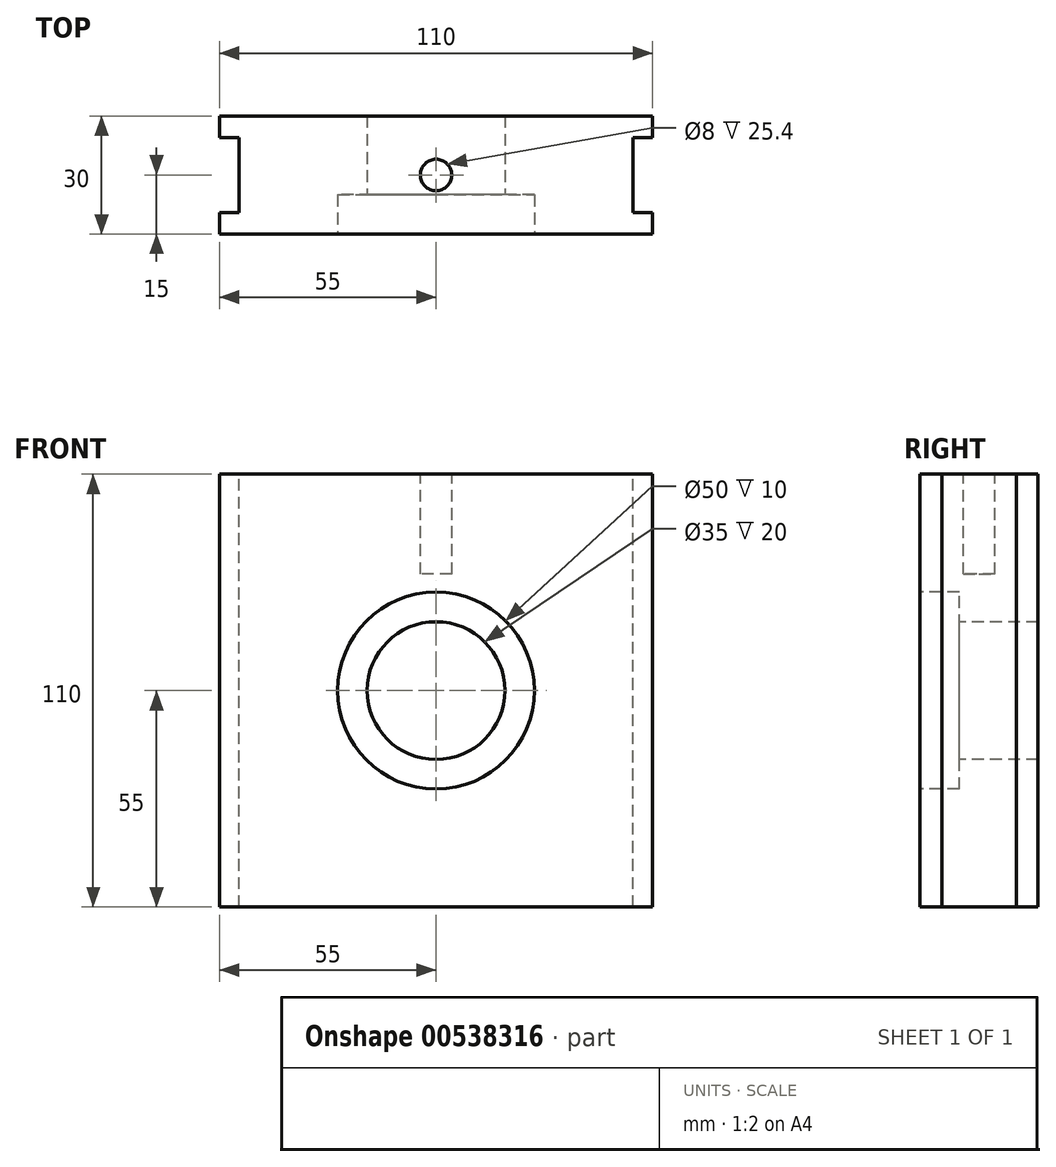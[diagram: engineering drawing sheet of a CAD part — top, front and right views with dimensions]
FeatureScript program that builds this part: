
annotation { "Feature Type Name" : "Feature", "Feature Type Description" : "" }
export const myFeature = defineFeature(function(context is Context, id is Id, definition is map)
    precondition{}
    {
        {
            var Q0;
            Q0=qCreatedBy(makeId("Front.planeOp"),FACE);
            var sketch = newSketch(context, id + "F0", { "sketchPlane" : qUnion([Q0])});
            skLineSegment(sketch, "E0.bottom", {"start": v(55, -55) * mm, "end": v(-55, -55) * mm});
            skLineSegment(sketch, "E0.top", {"start": v(55, 55) * mm, "end": v(-55, 55) * mm});
            skLineSegment(sketch, "E0.left", {"start": v(55, -55) * mm, "end": v(55, 55) * mm});
            skLineSegment(sketch, "E0.right", {"start": v(-55, -55) * mm, "end": v(-55, 55) * mm});
            skPoint(sketch, "E0.middle", {"position": v(0, 0) * mm});
            skSolve(sketch);
        }
        {
            var Q0;
            Q0 = qSketchRegion(id + "F0", true);
            extrude(context, id + "F1", {"entities" : qUnion([Q0]), "depth" : 30 * mm, "offsetDistance" : 25.4 * mm});
        }
        {
            var Q0;
            Q0=makeQuery(id+"F1.opExtrude","CAP_FACE",FACE,{"disambiguationData":[OSD([sQuery(id+"F0.wireOp",EDGE,"E0.bottom"),sQuery(id+"F0.wireOp",EDGE,"E0.top"),sQuery(id+"F0.wireOp",EDGE,"E0.left"),sQuery(id+"F0.wireOp",EDGE,"E0.right")])],"isStart":false});
            var sketch = newSketch(context, id + "F2", { "sketchPlane" : qUnion([Q0])});
            skCircle(sketch, "E1", {"center": v(0, 0) * mm, "radius": 25 * mm});
            skCircle(sketch, "E2", {"center": v(0, 0) * mm, "radius": 17.5 * mm});
            skSolve(sketch);
        }
        {
            var Q0;
            Q0 = qSketchRegion(id + "F2", true);
            var Q1;
            Q1=makeQuery(id+"F2.imprint","IMPRINT",FACE,{"disambiguationData":[TD([[makeQuery(id+"F2.imprint","IMPRINT",EDGE,{"derivedFrom":sQuery(id+"F2.wireOp",EDGE,"E1")}),1.0]])]});
            extrude(context, id + "F3", {"entities" : qUnion([Q0, Q1]), "operationType" : NewBodyOperationType.REMOVE, "oppositeDirection" : true, "depth" : 10 * mm, "offsetDistance" : 25.4 * mm});
        }
        {
            var Q0;
            Q0=makeQuery(id+"F3.boolean.opBoolean","SPLIT",FACE,{"disambiguationData":[TD([makeQuery(id+"F3.opExtrude","SWEPT_FACE",FACE,{"disambiguationData":[OSD([sQuery(id+"F2.wireOp",EDGE,"E2")])]})])],"derivedFrom":makeQuery(id+"F1.opExtrude","CAP_FACE",FACE,{"disambiguationData":[OSD([sQuery(id+"F0.wireOp",EDGE,"E0.bottom"),sQuery(id+"F0.wireOp",EDGE,"E0.top"),sQuery(id+"F0.wireOp",EDGE,"E0.left"),sQuery(id+"F0.wireOp",EDGE,"E0.right")])],"isStart":false})});
            extrude(context, id + "F4", {"entities" : qUnion([Q0]), "operationType" : NewBodyOperationType.REMOVE, "endBound" : BoundingType.THROUGH_ALL, "oppositeDirection" : true, "depth" : 25.4 * mm, "offsetDistance" : 25.4 * mm});
        }
        {
            var Q0;
            Q0=makeQuery(id+"F1.opExtrude","SWEPT_FACE",FACE,{"disambiguationData":[OSD([sQuery(id+"F0.wireOp",EDGE,"E0.top")])]});
            var sketch = newSketch(context, id + "F5", { "sketchPlane" : qUnion([Q0])});
            skLineSegment(sketch, "E3.bottom", {"start": v(-60, -24.5) * mm, "end": v(-50, -24.5) * mm});
            skLineSegment(sketch, "E3.top", {"start": v(-60, -5.5) * mm, "end": v(-50, -5.5) * mm});
            skLineSegment(sketch, "E3.left", {"start": v(-60, -24.5) * mm, "end": v(-60, -5.5) * mm});
            skLineSegment(sketch, "E3.right", {"start": v(-50, -24.5) * mm, "end": v(-50, -5.5) * mm});
            skPoint(sketch, "E3.middle", {"position": v(-55, -15) * mm});
            skLineSegment(sketch, "E4", {"start": v(0, 0) * mm, "end": v(0, -75.15) * mm, "construction": true});
            skPoint(sketch, "E5.MirrorP", {"position": v(55, -15) * mm});
            skLineSegment(sketch, "E6.MirrorCS", {"start": v(60, -24.5) * mm, "end": v(50, -24.5) * mm});
            skLineSegment(sketch, "E7.MirrorCS", {"start": v(60, -5.5) * mm, "end": v(50, -5.5) * mm});
            skLineSegment(sketch, "E8.MirrorCS", {"start": v(50, -24.5) * mm, "end": v(50, -5.5) * mm});
            skLineSegment(sketch, "E9.MirrorCS", {"start": v(60, -24.5) * mm, "end": v(60, -5.5) * mm});
            skSolve(sketch);
        }
        {
            var Q0;
            Q0 = qSketchRegion(id + "F5", true);
            extrude(context, id + "F6", {"entities" : qUnion([Q0]), "operationType" : NewBodyOperationType.REMOVE, "endBound" : BoundingType.THROUGH_ALL, "oppositeDirection" : true, "depth" : 25.4 * mm, "offsetDistance" : 25.4 * mm});
        }
        {
            var Q0;
            Q0=makeQuery(id+"F1.opExtrude","SWEPT_FACE",FACE,{"disambiguationData":[OSD([sQuery(id+"F0.wireOp",EDGE,"E0.top")])]});
            var sketch = newSketch(context, id + "F7", { "sketchPlane" : qUnion([Q0])});
            skCircle(sketch, "E10", {"center": v(0, -15) * mm, "radius": 4 * mm});
            skPoint(sketch, "E10.centerSnap0", {"position": v(50, -15) * mm});
            skPoint(sketch, "E10.centerSnap1", {"position": v(0, -30) * mm});
            skSolve(sketch);
        }
        {
            var Q0;
            Q0 = qSketchRegion(id + "F7", true);
            extrude(context, id + "F8", {"entities" : qUnion([Q0]), "operationType" : NewBodyOperationType.REMOVE, "oppositeDirection" : true, "depth" : 25.4 * mm, "offsetDistance" : 25.4 * mm});
        }
    });
